# Revit family: EU_SINGLE_IDU_BIG_CEILING_L_Ver.1.1
name_source: partatom
category: Mechanical Equipment
revit_build: Autodesk Revit 2016 (Build: 20150220_1215(x64)
units: mm (PartAtom-declared; Revit-internal decimal feet)

## family parameters
Always vertical = Yes
Cut with Voids When Loaded = No
OmniClass Number = 23.75.00.00
OmniClass Title = Climate Control (HVAC)
Part Type = Normal
Room Calculation Point = No
Round Connector Dimension = Use Diameter
Shared = No
Work Plane-Based = No

## types (10) — shared parameters
Manufacturer = SAMSUNG
Panel  Net Weight = 0.00 kg
Panel Model = -
URL = www.samsung.com

## per-type parameters (varying)
| type | Model | Motor Output | Net  Weight | Refrigerant Type |
| 10.00 kW,  220-240V, BIG CEILING | AC100MNCDKH/EU | 40 W | 41.40 kg | R410A |
| 12.00 kW,  220-240V, BIG CEILING | AC120MNCDKH/EU | 40 W | 41.40 kg | R410A |
| 13.40 kW,  220-240V, BIG CEILING | AC140MNCDKH/EU | 40 W | 41.40 kg | R410A |
| 15.00 kW,  220-240V, BIG CEILING | AC160JNCDEH/EU | 244 W | 42.00 kg | R410A |
| 10.0kW, 220-240V, Big_Ceiling_L, R32, 1Phase ODU | AC100RNCDKG/EU | 244 W | 41.40 kg | R32 |
| 10.0kW, 220-240V, Big_Ceiling_L, R32, 3Phase ODU | AC100RNCDKG/EU | 244 W | 41.40 kg | R32 |
| 12.0kW, 220-240V, Big_Ceiling_L, R32, 1Phase ODU | AC120RNCDKG/EU | 244 W | 41.50 kg | R32 |
| 12.0kW, 220-240V, Big_Ceiling_L, R32, 3Phase ODU | AC120RNCDKG/EU | 244 W | 41.50 kg | R32 |
| 14.0kW, 220-240V, Big_Ceiling_L, R32, 1Phase ODU | AC140RNCDKG/EU | 244 W | 41.50 kg | R32 |
| 14.0kW, 220-240V, Big_Ceiling_L, R32, 3Phase ODU | AC140RNCDKG/EU | 244 W | 41.50 kg | R32 |
